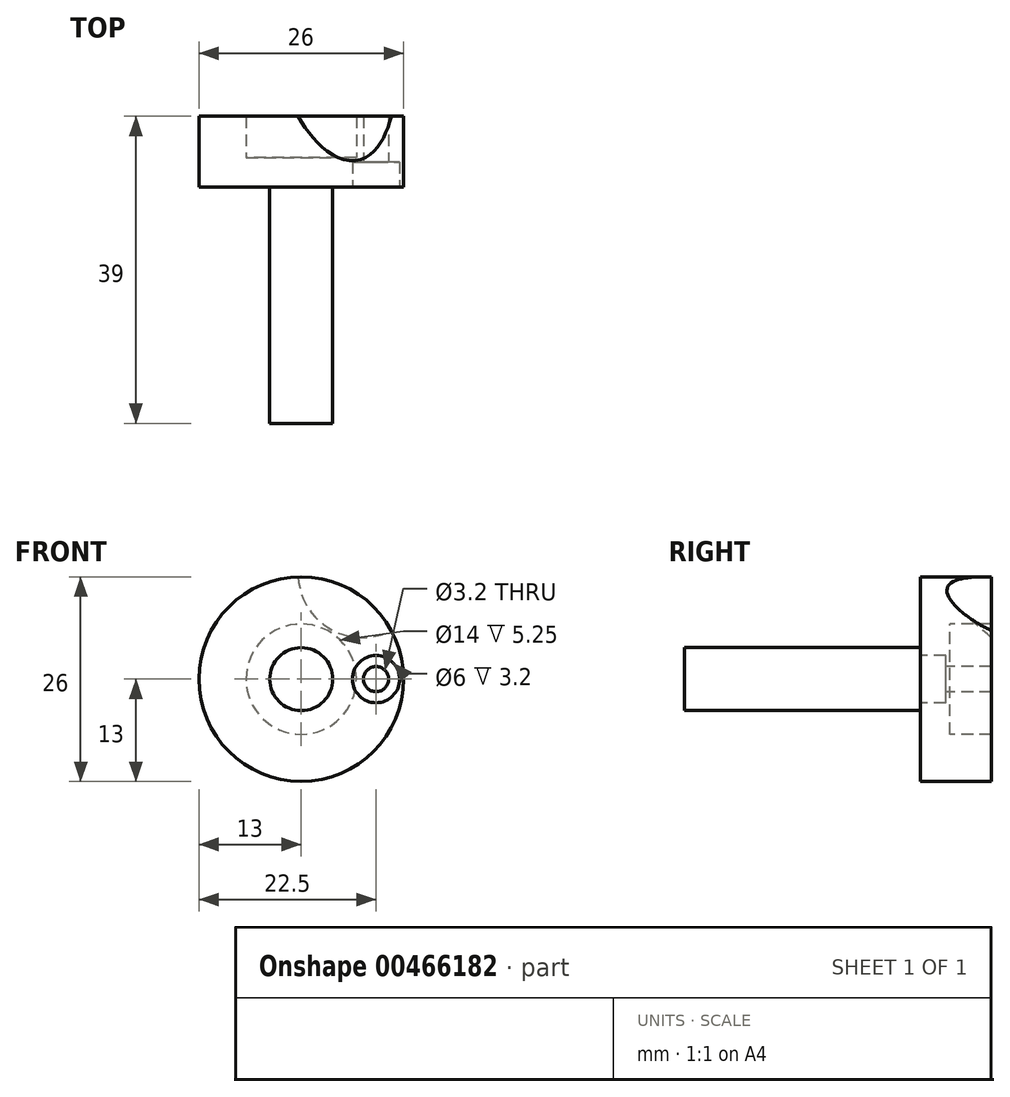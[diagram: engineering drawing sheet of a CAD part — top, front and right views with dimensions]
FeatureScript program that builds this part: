
annotation { "Feature Type Name" : "Feature", "Feature Type Description" : "" }
export const myFeature = defineFeature(function(context is Context, id is Id, definition is map)
    precondition{}
    {
        {
            var Q0;
            Q0=qCreatedBy(makeId("Right.planeOp"),FACE);
            var sketch = newSketch(context, id + "F0", { "sketchPlane" : qUnion([Q0])});
            skLineSegment(sketch, "E0", {"start": v(0, 0) * mm, "end": v(0, 7) * mm});
            skLineSegment(sketch, "E1", {"start": v(0, 7) * mm, "end": v(5.25, 7) * mm});
            skLineSegment(sketch, "E2", {"start": v(5.25, 7) * mm, "end": v(5.25, 13) * mm});
            skLineSegment(sketch, "E3", {"start": v(5.25, 13) * mm, "end": v(-3.75, 13) * mm});
            skLineSegment(sketch, "E4", {"start": v(-3.75, 13) * mm, "end": v(-3.75, 4) * mm});
            skLineSegment(sketch, "E5", {"start": v(-3.75, 4) * mm, "end": v(-33.75, 4) * mm});
            skLineSegment(sketch, "E6", {"start": v(-33.75, 4) * mm, "end": v(-33.75, 0) * mm});
            skLineSegment(sketch, "E7", {"start": v(-33.75, 0) * mm, "end": v(0, 0) * mm});
            skSolve(sketch);
        }
        {
            var Q0;
            Q0=makeQuery(id+"F0.imprint","IMPRINT",FACE,{"disambiguationData":[TD([[makeQuery(id+"F0.imprint","IMPRINT",EDGE,{"derivedFrom":sQuery(id+"F0.wireOp",EDGE,"E0")}),1.0]])]});
            var Q1;
            Q1=sQuery(id+"F0.wireOp",EDGE,"E7");
            revolve(context, id + "F1", {"entities" : qUnion([Q0]), "axis" : qUnion([Q1]), "revolveType" : RevolveType.FULL});
        }
        {
            var Q0;
            Q0=makeQuery(id+"F1.opRevolve","SWEPT_FACE",FACE,{"disambiguationData":[OSD([sQuery(id+"F0.wireOp",EDGE,"E4")])]});
            cPlane(context, id + "F2", {"entities" : qUnion([Q0]), "cplaneType" : CPlaneType.OFFSET, "offset" : 8 * mm, "width" : 150 * mm, "height" : 150 * mm});
        }
        {
            var Q0;
            Q0=qCreatedBy(id+"F2.planeOp",FACE);
            var sketch = newSketch(context, id + "F3", { "sketchPlane" : qUnion([Q0])});
            skCircle(sketch, "E8", {"center": v(0, 0) * mm, "radius": 4 * mm});
            skSolve(sketch);
        }
        {
            var Q0;
            Q0=makeQuery(id+"F1.opRevolve","SWEPT_FACE",FACE,{"disambiguationData":[OSD([sQuery(id+"F0.wireOp",EDGE,"E4")])]});
            var sketch = newSketch(context, id + "F4", { "sketchPlane" : qUnion([Q0])});
            skCircle(sketch, "E9", {"center": v(9.5, 0) * mm, "radius": 1.6 * mm});
            skSolve(sketch);
        }
        {
            var Q0;
            Q0=makeQuery(id+"F4.imprint","IMPRINT",FACE,{"disambiguationData":[TD([[makeQuery(id+"F4.imprint","IMPRINT",EDGE,{"derivedFrom":sQuery(id+"F4.wireOp",EDGE,"E9")}),1.0]])]});
            extrude(context, id + "F5", {"entities" : qUnion([Q0]), "operationType" : NewBodyOperationType.REMOVE, "endBound" : BoundingType.THROUGH_ALL, "oppositeDirection" : true, "depth" : 25 * mm, "offsetDistance" : 25 * mm});
        }
        {
            var Q0;
            Q0=makeQuery(id+"F1.opRevolve","SWEPT_FACE",FACE,{"disambiguationData":[OSD([sQuery(id+"F0.wireOp",EDGE,"E4")])]});
            var sketch = newSketch(context, id + "F6", { "sketchPlane" : qUnion([Q0])});
            skCircle(sketch, "E10", {"center": v(9.5, 0) * mm, "radius": 3 * mm});
            skSolve(sketch);
        }
        {
            var Q0;
            Q0=makeQuery(id+"F6.imprint","IMPRINT",FACE,{"disambiguationData":[TD([[makeQuery(id+"F6.imprint","IMPRINT",EDGE,{"derivedFrom":sQuery(id+"F6.wireOp",EDGE,"E10")}),1.0]])]});
            extrude(context, id + "F7", {"entities" : qUnion([Q0]), "operationType" : NewBodyOperationType.REMOVE, "oppositeDirection" : true, "depth" : 3.2 * mm, "offsetDistance" : 25 * mm});
        }
        {
            var Q0;
            Q0=makeQuery(id+"F1.opRevolve","SWEPT_FACE",FACE,{"disambiguationData":[OSD([sQuery(id+"F0.wireOp",EDGE,"E2")])]});
            var sketch = newSketch(context, id + "F8", { "sketchPlane" : qUnion([Q0])});
            skArc(sketch, "E11", {"start": v(-11.44, 6.17) * mm, "mid": v(-3.68, 6.37) * mm, "end": v(0.38, 13) * mm});
            skLineSegment(sketch, "E12", {"start": v(-11.44, 6.17) * mm, "end": v(0.38, 13) * mm, "construction": true});
            skLineSegment(sketch, "E13", {"start": v(-9.5, 0) * mm, "end": v(4.75, 8.23) * mm, "construction": true});
            skArc(sketch, "E14", {"start": v(-11.44, 6.17) * mm, "mid": v(-11.8, 20.44) * mm, "end": v(0.38, 13) * mm});
            skSolve(sketch);
        }
        {
            var Q0;
            Q0=makeQuery(id+"F1.opRevolve","SWEPT_FACE",FACE,{"disambiguationData":[OSD([sQuery(id+"F0.wireOp",EDGE,"E4")])]});
            var sketch = newSketch(context, id + "F9", { "sketchPlane" : qUnion([Q0])});
            skLineSegment(sketch, "E15", {"start": v(-4.75, 8.23) * mm, "end": v(9.5, 0) * mm, "construction": true});
            skSolve(sketch);
        }
        {
            var Q0;
            Q0=sQuery(id+"F9.wireOp",EDGE,"E15");
            cPlane(context, id + "F10", {"entities" : qUnion([Q0]), "cplaneType" : CPlaneType.LINE_ANGLE, "offset" : 25 * mm, "angle" : 45 * degree, "oppositeDirection" : true, "width" : 150 * mm, "height" : 150 * mm});
        }
        {
            var Q0;
            Q0=qCreatedBy(id+"F10.planeOp",FACE);
            var sketch = newSketch(context, id + "F11", { "sketchPlane" : qUnion([Q0])});
            skEllipticalArc(sketch, "E16.0.0", {});
            skEllipticalArc(sketch, "E16.0.1", {});
            const initialGuessF11  = {"E16.0.0": [-0.0014031215200402281, 0.0034369317712168793, 0.9258200997725515, 0.3779644730092274, 0.013, 0.009192388155425122, 1.0180812136981139, 2.12351143989168], "E16.0.1": [-0.0055396734919024035, 0.013569373396782797, 0.9258200997725515, 0.3779644730092274, 0.008127560241292403, 0.0057470529611200315, 3.7155932497396393, 5.7091847110297405]};
            skSetInitialGuess(sketch, initialGuessF11);
            skSolve(sketch);
        }
        {
            var Q0;
            Q0=makeQuery(id+"F11.imprint","IMPRINT",FACE,{"disambiguationData":[TD([[makeQuery(id+"F11.imprint","IMPRINT",EDGE,{"derivedFrom":sQuery(id+"F11.wireOp",EDGE,"E16.0.0")}),1.0]])]});
            extrude(context, id + "F12", {"entities" : qUnion([Q0]), "operationType" : NewBodyOperationType.REMOVE, "endBound" : BoundingType.THROUGH_ALL, "oppositeDirection" : true, "depth" : 25 * mm, "offsetDistance" : 25 * mm, "hasSecondDirection" : true, "secondDirectionBound" : SecondDirectionBoundingType.THROUGH_ALL, "secondDirectionOppositeDirection" : false, "secondDirectionDepth" : 25 * mm});
        }
    });
